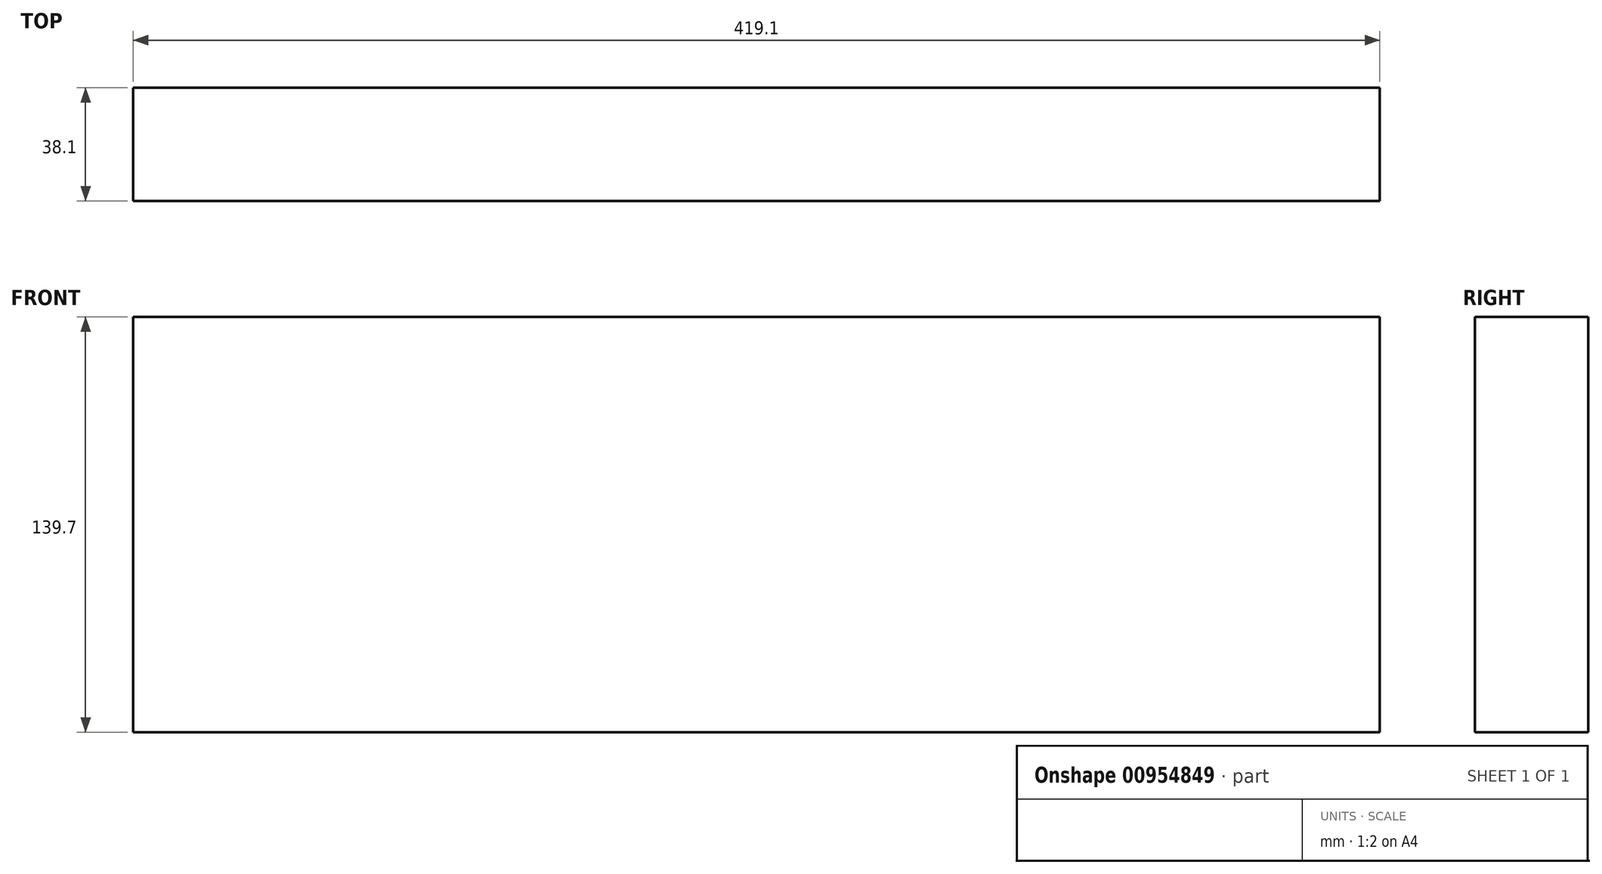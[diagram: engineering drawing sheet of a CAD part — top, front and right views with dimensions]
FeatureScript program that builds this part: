
annotation { "Feature Type Name" : "Feature", "Feature Type Description" : "" }
export const myFeature = defineFeature(function(context is Context, id is Id, definition is map)
    precondition{}
    {
        {
            var Q0;
            Q0=qCreatedBy(makeId("Right.planeOp"),FACE);
            var sketch = newSketch(context, id + "F0", { "sketchPlane" : qUnion([Q0])});
            skLineSegment(sketch, "E0.bottom", {"start": v(-19.05, 69.85) * mm, "end": v(19.05, 69.85) * mm});
            skLineSegment(sketch, "E0.top", {"start": v(-19.05, -69.85) * mm, "end": v(19.05, -69.85) * mm});
            skLineSegment(sketch, "E0.left", {"start": v(-19.05, 69.85) * mm, "end": v(-19.05, -69.85) * mm});
            skLineSegment(sketch, "E0.right", {"start": v(19.05, 69.85) * mm, "end": v(19.05, -69.85) * mm});
            skPoint(sketch, "E1", {"position": v(0, 69.85) * mm});
            skPoint(sketch, "E2", {"position": v(-19.05, 0) * mm});
            skSolve(sketch);
        }
        {
            var Q0;
            Q0=qSketchRegion(id+"F0",true);
            extrude(context, id + "F1", {"entities" : qUnion([Q0]), "depth" : 419.1 * mm, "offsetDistance" : 25.4 * mm});
        }
    });
